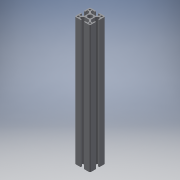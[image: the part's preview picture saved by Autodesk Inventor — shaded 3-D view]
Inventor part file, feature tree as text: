
AUTODESK INVENTOR PART (.ipt)
format: ipt  version: 2018 (Build 220112000, 112)  size: 201,728 bytes
history: native  units: mm
features: other x42, sketch x5, hole x4, extrude x1
ambient origin geometry x8: Origin, YZ Plane, XZ Plane, XY Plane, X Axis, Y Axis, Z Axis, Center Point
bodies: Solid1 (feature_tree)
feature tree (52):
  extrude  "Extrusion1"  [1 undecoded]
  hole  "Drilling 1"  [1 undecoded]
  hole  "Drilling 2"  [1 undecoded]
  hole  "Drilling 3"  [1 undecoded]
  hole  "Drilling 4"  [1 undecoded]
  other  "side_4d_XY"
  other  "side_4d_YZ"
  other  "side_4d_ZX"
  other  "side_4d_X"
  other  "side_4d_Y"
  other  "side_4d_Z"
  other  "side_4d_Center"
  other  "side_1a_XY"
  other  "side_1a_YZ"
  other  "side_1a_ZX"
  other  "side_1a_X"
  other  "side_1a_Y"
  other  "side_1a_Z"
  other  "side_1a_Center"
  other  "side_2b_XY"
  other  "side_2b_YZ"
  other  "side_2b_ZX"
  other  "side_2b_X"
  other  "side_2b_Y"
  other  "side_2b_Z"
  other  "side_2b_Center"
  other  "side_3c_XY"
  other  "side_3c_YZ"
  other  "side_3c_ZX"
  other  "side_3c_X"
  other  "side_3c_Y"
  other  "side_3c_Z"
  other  "side_3c_Center"
  other  "end_XY"
  other  "end_YZ"
  other  "end_ZX"
  other  "end_X"
  other  "end_Y"
  other  "end_Z"
  other  "end_Center"
  other  "start_XY"
  other  "start_YZ"
  other  "start_ZX"
  other  "start_X"
  other  "start_Y"
  other  "start_Z"
  other  "start_Center"
  sketch  "Skizze_1"  dims[d0=330.0mm d1=0.0mm]
  sketch  "Sketch2"  dims[d2=5.0mm d3=6.0mm d4=4.0mm d5=2.0mm d6=90.0deg d7=6000.0mm d8=0.0mm]
  sketch  "Sketch3"  dims[d9=5.0mm d10=6.0mm d11=4.0mm d12=2.0mm d13=90.0deg d14=6000.0mm d15=0.0mm]
  sketch  "Sketch4"  dims[d16=5.0mm d17=6.0mm d18=4.0mm d19=2.0mm d20=90.0deg d21=6000.0mm d22=0.0mm]
  sketch  "Sketch5"  dims[d23=5.0mm d24=6.0mm d25=4.0mm d26=2.0mm d27=90.0deg d28=6000.0mm d29=0.0mm]
note: 5 required parameter values undecoded (feature->parameter linkage not recoverable at this tier; creation-order binding heuristic only, values carry confidence <= 0.55)
